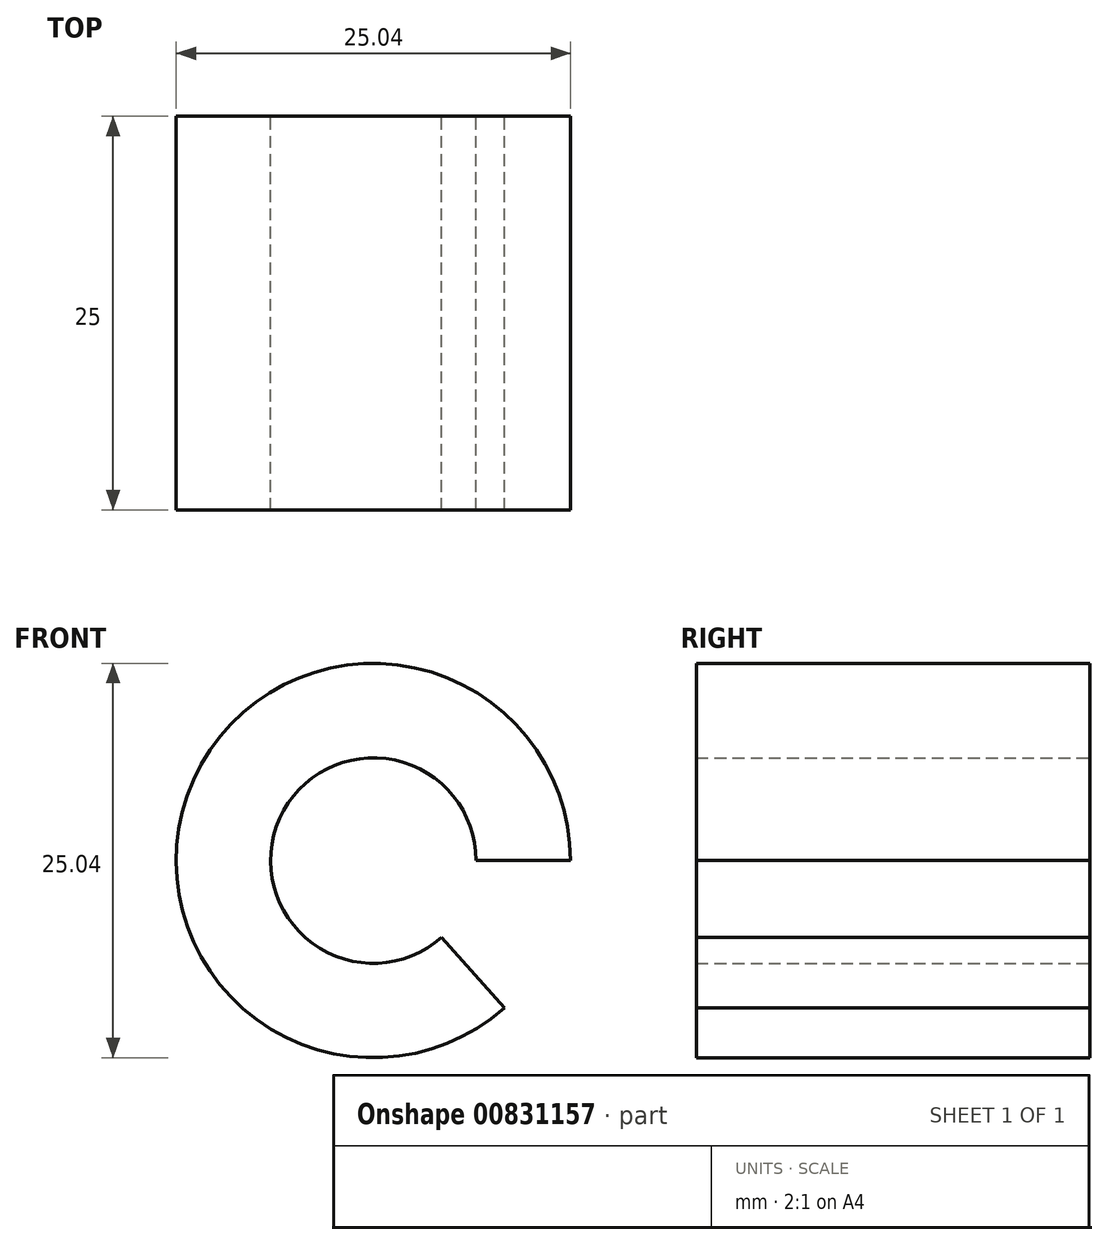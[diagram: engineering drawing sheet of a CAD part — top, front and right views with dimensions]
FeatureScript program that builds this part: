
annotation { "Feature Type Name" : "Feature", "Feature Type Description" : "" }
export const myFeature = defineFeature(function(context is Context, id is Id, definition is map)
    precondition{}
    {
        {
            var Q0;
            Q0=qCreatedBy(makeId("Front.planeOp"),FACE);
            var sketch = newSketch(context, id + "F0", { "sketchPlane" : qUnion([Q0])});
            skCircle(sketch, "E0", {"center": v(0, 0) * mm, "radius": 6.52 * mm});
            skCircle(sketch, "E1.0", {"center": v(0, 0) * mm, "radius": 12.52 * mm});
            skLineSegment(sketch, "E2", {"start": v(-12.52, 0) * mm, "end": v(12.52, 0) * mm});
            skLineSegment(sketch, "E3", {"start": v(0, 12.52) * mm, "end": v(0, -12.52) * mm});
            skLineSegment(sketch, "E4", {"start": v(-9.34, -8.35) * mm, "end": v(9.34, 8.35) * mm});
            skLineSegment(sketch, "E5", {"start": v(-8.33, 9.35) * mm, "end": v(8.33, -9.35) * mm});
            skSolve(sketch);
        }
        {
            var Q0;
            {var subQ0=sQuery(id+"F0.wireOp",EDGE,"E3");var subQ1=sQuery(id+"F0.wireOp",EDGE,"E0");var subQ2=makeQuery(id+"F0.imprint","INTERSECT",VERTEX,{"disambiguationData":[OD(0.0)],"derivedFrom":[subQ1,subQ0]});Q0=makeQuery(id+"F0.imprint","IMPRINT",FACE,{"disambiguationData":[TD([[makeQuery(id+"F0.imprint","IMPRINT",EDGE,{"disambiguationData":[TD([[subQ2,-1.0]])],"derivedFrom":subQ1}),-1.0]])]});}
            var Q1;
            {var subQ0=sQuery(id+"F0.wireOp",EDGE,"E5");var subQ1=sQuery(id+"F0.wireOp",EDGE,"E0");var subQ2=makeQuery(id+"F0.imprint","INTERSECT",VERTEX,{"disambiguationData":[OD(0.0)],"derivedFrom":[subQ1,subQ0]});Q1=makeQuery(id+"F0.imprint","IMPRINT",FACE,{"disambiguationData":[TD([[makeQuery(id+"F0.imprint","IMPRINT",EDGE,{"disambiguationData":[TD([[subQ2,-1.0]])],"derivedFrom":subQ1}),-1.0]])]});}
            var Q2;
            {var subQ0=sQuery(id+"F0.wireOp",EDGE,"E2");var subQ1=sQuery(id+"F0.wireOp",EDGE,"E0");var subQ2=makeQuery(id+"F0.imprint","INTERSECT",VERTEX,{"disambiguationData":[OD(1.0)],"derivedFrom":[subQ1,subQ0]});Q2=makeQuery(id+"F0.imprint","IMPRINT",FACE,{"disambiguationData":[TD([[makeQuery(id+"F0.imprint","IMPRINT",EDGE,{"disambiguationData":[TD([[subQ2,-1.0]])],"derivedFrom":subQ1}),-1.0]])]});}
            var Q3;
            {var subQ0=sQuery(id+"F0.wireOp",EDGE,"E4");var subQ1=sQuery(id+"F0.wireOp",EDGE,"E0");var subQ2=makeQuery(id+"F0.imprint","INTERSECT",VERTEX,{"disambiguationData":[OD(1.0)],"derivedFrom":[subQ1,subQ0]});Q3=makeQuery(id+"F0.imprint","IMPRINT",FACE,{"disambiguationData":[TD([[makeQuery(id+"F0.imprint","IMPRINT",EDGE,{"disambiguationData":[TD([[subQ2,-1.0]])],"derivedFrom":subQ1}),-1.0]])]});}
            var Q4;
            {var subQ0=sQuery(id+"F0.wireOp",EDGE,"E3");var subQ1=sQuery(id+"F0.wireOp",EDGE,"E0");var subQ2=makeQuery(id+"F0.imprint","INTERSECT",VERTEX,{"disambiguationData":[OD(1.0)],"derivedFrom":[subQ1,subQ0]});Q4=makeQuery(id+"F0.imprint","IMPRINT",FACE,{"disambiguationData":[TD([[makeQuery(id+"F0.imprint","IMPRINT",EDGE,{"disambiguationData":[TD([[subQ2,-1.0]])],"derivedFrom":subQ1}),-1.0]])]});}
            var Q5;
            {var subQ0=sQuery(id+"F0.wireOp",EDGE,"E4");var subQ1=sQuery(id+"F0.wireOp",EDGE,"E0");var subQ2=makeQuery(id+"F0.imprint","INTERSECT",VERTEX,{"disambiguationData":[OD(0.0)],"derivedFrom":[subQ1,subQ0]});Q5=makeQuery(id+"F0.imprint","IMPRINT",FACE,{"disambiguationData":[TD([[makeQuery(id+"F0.imprint","IMPRINT",EDGE,{"disambiguationData":[TD([[subQ2,1.0]])],"derivedFrom":subQ1}),-1.0]])]});}
            var Q6;
            {var subQ0=sQuery(id+"F0.wireOp",EDGE,"E4");var subQ1=sQuery(id+"F0.wireOp",EDGE,"E0");var subQ2=makeQuery(id+"F0.imprint","INTERSECT",VERTEX,{"disambiguationData":[OD(0.0)],"derivedFrom":[subQ1,subQ0]});Q6=makeQuery(id+"F0.imprint","IMPRINT",FACE,{"disambiguationData":[TD([[makeQuery(id+"F0.imprint","IMPRINT",EDGE,{"disambiguationData":[TD([[subQ2,-1.0]])],"derivedFrom":subQ1}),-1.0]])]});}
            var Q7;
            {var subQ0=sQuery(id+"F0.wireOp",EDGE,"E2");var subQ1=sQuery(id+"F0.wireOp",EDGE,"E0");var subQ2=makeQuery(id+"F0.imprint","INTERSECT",VERTEX,{"disambiguationData":[OD(0.0)],"derivedFrom":[subQ1,subQ0]});Q7=makeQuery(id+"F0.imprint","IMPRINT",FACE,{"disambiguationData":[TD([[makeQuery(id+"F0.imprint","IMPRINT",EDGE,{"disambiguationData":[TD([[subQ2,1.0]])],"derivedFrom":subQ1}),-1.0]])]});}
            extrude(context, id + "F1", {"entities" : qUnion([Q0, Q1, Q2, Q3, Q4, Q5, Q6, Q7]), "depth" : 25 * mm, "offsetDistance" : 25 * mm});
        }
    });
